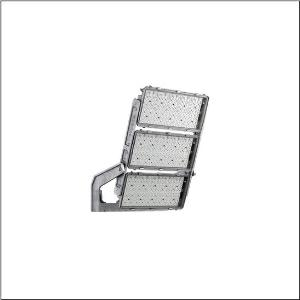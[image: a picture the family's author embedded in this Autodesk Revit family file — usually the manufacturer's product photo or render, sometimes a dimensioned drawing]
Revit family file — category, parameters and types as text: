
# Revit family: floodlight_fl_11_maxi_pro_remote___pl43_5xa779524a01ba_c92a
name_source: partatom
category: Lighting Fixtures
units: mm (PartAtom-declared; Revit-internal decimal feet)

## family parameters
Cut with Voids When Loaded = No
Host = Face
Light Source = No
Part Type = Normal
Room Calculation Point = No
Round Connector Dimension = Use Diameter
Shared = No

## types (1)
- --- (1 x LED, 108940 lm, 1020.5 W, 5700K)
    Apparent Load = 1020 VA
    CIE Flux Codes = 25 74 99 100 100
    Color Rendering = 90
    Color Temperature = 5700K
    Default Elevation = 1800 mm
    Description = Floodlight FL 11  maxi  pro Remote floodlight; light control with lens of PMMA; cover panel of toughened safety glass, transparent; light distribution: PL43, asymmetric direct distribution, LEDcolour temperature: 5700K, rated luminous flux: 108.940lm, colour rendering: CRI > 90, light colour: 957; luminous efficacy: 107lm/W; brightness control: DMX+RDM; with terminal, 8-pole, max. 2.5mm², mains connection: 220..240V/380..400V AC, 50/60Hz, surge voltage resistance: line to ground: 10kV, ECG replaceable separately, LED unit replaceable without ESD environment, dustproof LED module, dimming range 10..100%; 1021W floodlight with 3x LED unit of diecast aluminium, coated grey; length: 713mm / width: 651mm / height: 338mm; mounting bracket, of diecast aluminium, uncoated, natural, equipment: Longlife, protection rating (complete): IP66; insulation class (complete): insulation class I (protective earthing); certification: CE, ENEC, VDE; ball protection: ball impact resistance with accessories, impact resistance: IK07; only for outdoor installations, rated ambient temperature 10°C, permissible operating ambient temperature: -40..+40°C, permissible storage temperature: -40..+85°C; packaging unit: 1 piece

Light Distribution: PL43
    Height = 320 mm
    Lamp = 1 x LED
    Lamp Light Flux = 108940 lm
    Lamp Power = 1020.5 W
    Lamp count = 1
    Length = 1002 mm
    Luminous efficacy = 107 lm/W
    Manufacturer = Siteco
    ModVariant = No
    Model = 5XA779524A01BA
    Mounting Place = Ceiling
    Mounting Type = Surface mounted
    Number of Poles = 1
    OnlyDefault = Yes
    Power Factor = 1
    Product Name = Floodlight FL 11 maxi pro Remote | PL43
    Product group = floodlight | ceiling mounted
    ProductGroupID = 302
    Protection Class = Protection class I
    Protection Degree = IP 66
    RLX_Detail_Level = 1
    RLX_Emergency_Light_Flux = 0 lm
    RLX_Emergency_Type = 0
    RLX_Emergency_Type_DB = No
    RlxData = <blob elided: 52437 chars, md5=2aee9b03>
    Socket = socket
    Standby Power = 0 W
    System Light Flux = 108940 lm
    System Power = 1020 W
    Type Comments = factory setting: luminous flux: 100 % | dim-lin: 255 | 710 mA
    Type Image = l_1006784.jpg
    URL = http://relux.com
    VarID = @adj_065401
    Voltage = 0 V
    Weight = 0.00 kg
    Width = 655 mm

## geometry (parser evidence)
native form markers: Blend x4, Sweep x14
no freeform markers — native parametric forms only
